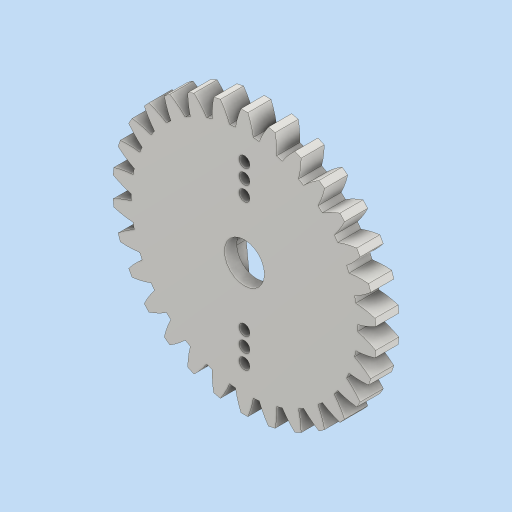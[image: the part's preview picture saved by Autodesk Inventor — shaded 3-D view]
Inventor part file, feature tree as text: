
AUTODESK INVENTOR PART (.ipt)
format: ipt  version: 2024 (Build 280153000, 153)  size: 340,992 bytes
history: native  units: mm (DEFAULTED — no unit token found)
features: extrude x3, plane x3, other x3, sketch x2
ambient origin geometry x8: Origin, YZ Plane, XZ Plane, XY Plane, X Axis, Y Axis, Z Axis, Center Point
bodies: Solid1 (feature_tree)
feature tree (11):
  extrude  "Extrusion1"  Depth=3.175mm TaperAngle=0.0deg
  plane  "Work Plane1"
  plane  "Work Plane2"
  plane  "Work Plane3"
  other  "Spur Gear"
  sketch  "Sketch3"  dims[d3=33.75mm d4=76.2mm d5=0.0mm d6=0.0mm d7=1.047198mm d9=0.0mm d14=0.0mm d15=25.4mm d16=0.0mm d17=0.0mm d18=0.0mm d19=25.4mm d20=3.0mm d21=3.0mm d22=24.0mm d23=5.5mm d24=0.2mm d27=1.5mm d28=1.0mm d29=1.5mm d30=1.5mm d31=1.0mm d32=1.0mm d33=1.0mm d34=1.0mm d35=20.0mm d37=360.0deg d39=1.5mm d40=0.0mm d41=0.0mm d42=0.0mm]
  extrude  "Extrusion2"  Depth=1.5mm TaperAngle=0.0deg
  extrude  "Extrusion3"  Depth=1.5mm TaperAngle=0.0deg
  sketch  "Sketch1"  dims[d0=36.178255mm d1=3.175mm d2=0.0mm]
  other  "Srf1"
  other  "Pitch Diameter"
